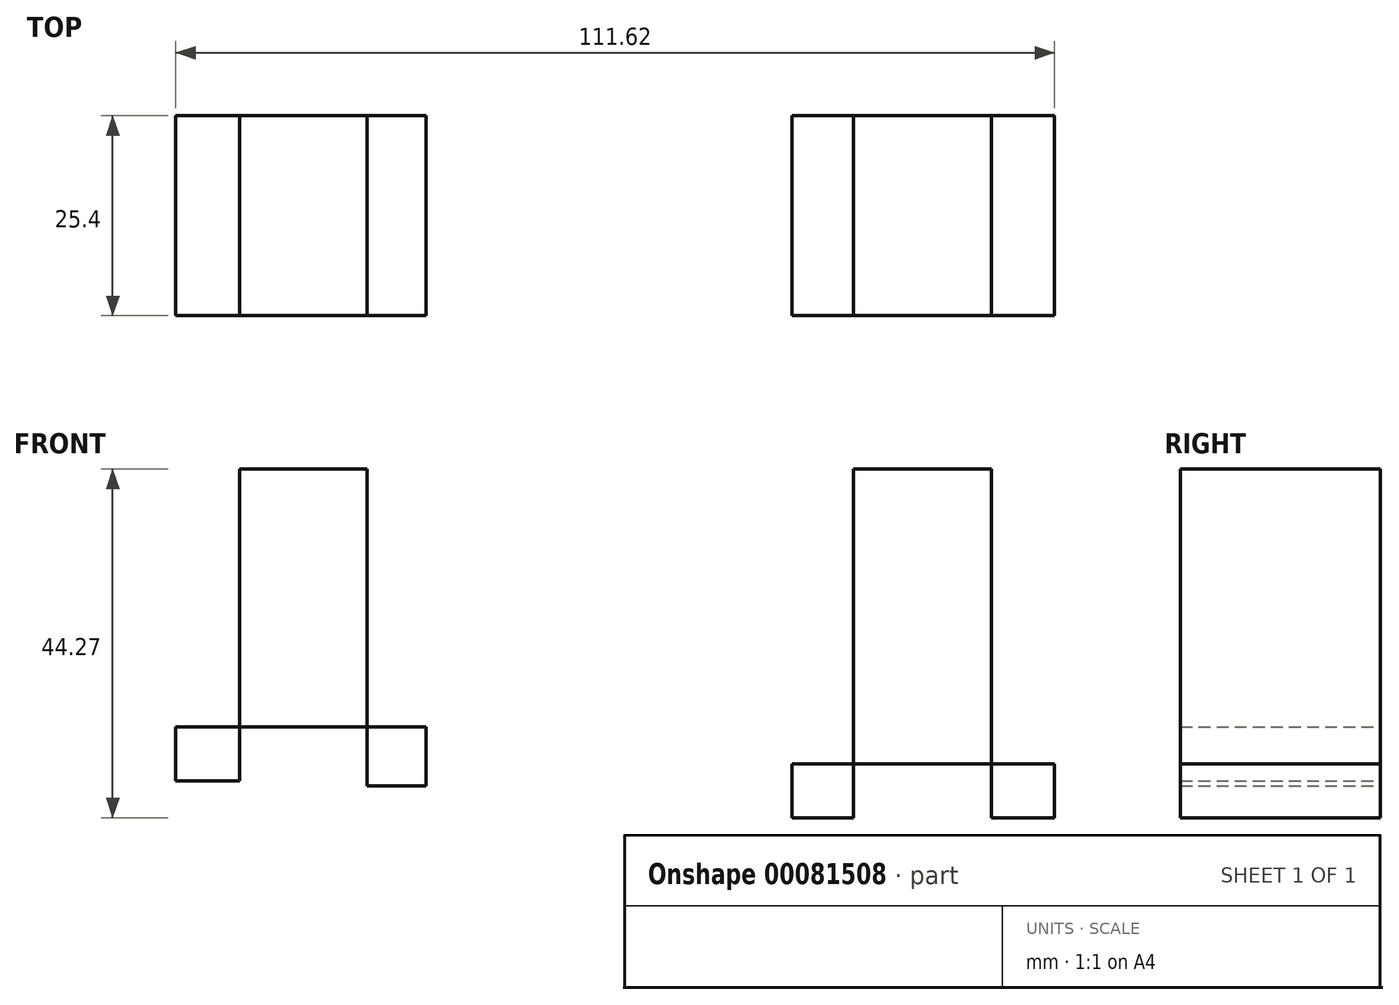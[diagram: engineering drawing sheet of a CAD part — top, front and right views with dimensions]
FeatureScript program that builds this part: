
annotation { "Feature Type Name" : "Feature", "Feature Type Description" : "" }
export const myFeature = defineFeature(function(context is Context, id is Id, definition is map)
    precondition{}
    {
        {
            var Q0;
            Q0=qCreatedBy(makeId("Front.planeOp"),FACE);
            var sketch = newSketch(context, id + "F0", { "sketchPlane" : qUnion([Q0])});
            skLineSegment(sketch, "E0.bottom", {"start": v(-51.45, 20.11) * mm, "end": v(-35.23, 20.11) * mm});
            skLineSegment(sketch, "E0.top", {"start": v(-51.45, -12.63) * mm, "end": v(-35.23, -12.63) * mm});
            skLineSegment(sketch, "E0.left", {"start": v(-51.45, 20.11) * mm, "end": v(-51.45, -12.63) * mm});
            skLineSegment(sketch, "E0.right", {"start": v(-35.23, 20.11) * mm, "end": v(-35.23, -12.63) * mm});
            skLineSegment(sketch, "E1.bottom", {"start": v(-51.45, -12.63) * mm, "end": v(-59.55, -12.63) * mm});
            skLineSegment(sketch, "E1.top", {"start": v(-51.45, -19.49) * mm, "end": v(-59.55, -19.49) * mm});
            skLineSegment(sketch, "E1.left", {"start": v(-51.45, -12.63) * mm, "end": v(-51.45, -19.49) * mm});
            skLineSegment(sketch, "E1.right", {"start": v(-59.55, -12.63) * mm, "end": v(-59.55, -19.49) * mm});
            skLineSegment(sketch, "E2.bottom", {"start": v(-35.23, -12.63) * mm, "end": v(-27.75, -12.63) * mm});
            skLineSegment(sketch, "E2.top", {"start": v(-35.23, -20.11) * mm, "end": v(-27.75, -20.11) * mm});
            skLineSegment(sketch, "E2.left", {"start": v(-35.23, -12.63) * mm, "end": v(-35.23, -20.11) * mm});
            skLineSegment(sketch, "E2.right", {"start": v(-27.75, -12.63) * mm, "end": v(-27.75, -20.11) * mm});
            skLineSegment(sketch, "E3.bottom", {"start": v(26.5, 20.11) * mm, "end": v(44.04, 20.11) * mm});
            skLineSegment(sketch, "E3.top", {"start": v(26.5, -17.3) * mm, "end": v(44.04, -17.3) * mm});
            skLineSegment(sketch, "E3.left", {"start": v(26.5, 20.11) * mm, "end": v(26.5, -17.3) * mm});
            skLineSegment(sketch, "E3.right", {"start": v(44.04, 20.11) * mm, "end": v(44.04, -17.3) * mm});
            skLineSegment(sketch, "E4.bottom", {"start": v(26.5, -17.3) * mm, "end": v(18.7, -17.3) * mm});
            skLineSegment(sketch, "E4.top", {"start": v(26.5, -24.16) * mm, "end": v(18.7, -24.16) * mm});
            skLineSegment(sketch, "E4.left", {"start": v(26.5, -17.3) * mm, "end": v(26.5, -24.16) * mm});
            skLineSegment(sketch, "E4.right", {"start": v(18.7, -17.3) * mm, "end": v(18.7, -24.16) * mm});
            skLineSegment(sketch, "E5.bottom", {"start": v(44.04, -17.3) * mm, "end": v(52.07, -17.3) * mm});
            skLineSegment(sketch, "E5.top", {"start": v(44.04, -24.16) * mm, "end": v(52.07, -24.16) * mm});
            skLineSegment(sketch, "E5.left", {"start": v(44.04, -17.3) * mm, "end": v(44.04, -24.16) * mm});
            skLineSegment(sketch, "E5.right", {"start": v(52.07, -17.3) * mm, "end": v(52.07, -24.16) * mm});
            skSolve(sketch);
        }
        {
            var Q0;
            Q0=makeQuery(id+"F0.imprint","IMPRINT",FACE,{"disambiguationData":[TD([[makeQuery(id+"F0.imprint","IMPRINT",EDGE,{"derivedFrom":sQuery(id+"F0.wireOp",EDGE,"E0.bottom")}),-1.0]])]});
            var Q1;
            Q1=makeQuery(id+"F0.imprint","IMPRINT",FACE,{"disambiguationData":[TD([[makeQuery(id+"F0.imprint","IMPRINT",EDGE,{"derivedFrom":sQuery(id+"F0.wireOp",EDGE,"E1.bottom")}),1.0]])]});
            var Q2;
            Q2=makeQuery(id+"F0.imprint","IMPRINT",FACE,{"disambiguationData":[TD([[makeQuery(id+"F0.imprint","IMPRINT",EDGE,{"derivedFrom":sQuery(id+"F0.wireOp",EDGE,"E2.bottom")}),-1.0]])]});
            var Q3;
            Q3=makeQuery(id+"F0.imprint","IMPRINT",FACE,{"disambiguationData":[TD([[makeQuery(id+"F0.imprint","IMPRINT",EDGE,{"derivedFrom":sQuery(id+"F0.wireOp",EDGE,"E4.bottom")}),1.0]])]});
            var Q4;
            Q4=makeQuery(id+"F0.imprint","IMPRINT",FACE,{"disambiguationData":[TD([[makeQuery(id+"F0.imprint","IMPRINT",EDGE,{"derivedFrom":sQuery(id+"F0.wireOp",EDGE,"E5.bottom")}),-1.0]])]});
            var Q5;
            Q5=makeQuery(id+"F0.imprint","IMPRINT",FACE,{"disambiguationData":[TD([[makeQuery(id+"F0.imprint","IMPRINT",EDGE,{"derivedFrom":sQuery(id+"F0.wireOp",EDGE,"E3.bottom")}),-1.0]])]});
            extrude(context, id + "F1", {"entities" : qUnion([Q0, Q1, Q2, Q3, Q4, Q5]), "depth" : 25.4 * mm});
        }
    });
